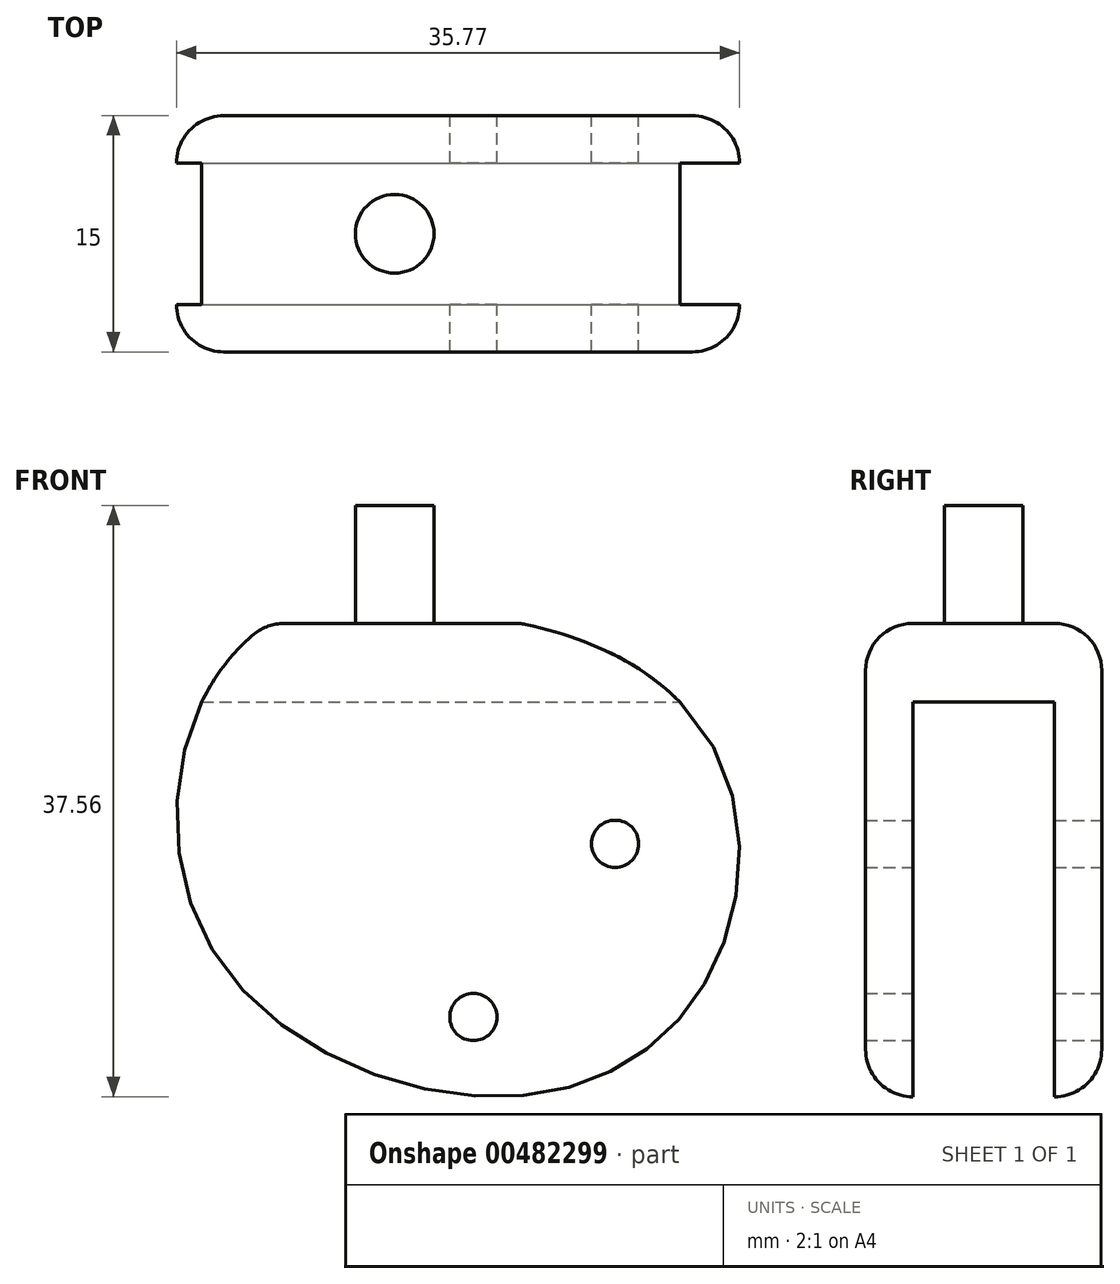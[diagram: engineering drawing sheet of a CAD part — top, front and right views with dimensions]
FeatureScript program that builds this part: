
annotation { "Feature Type Name" : "Feature", "Feature Type Description" : "" }
export const myFeature = defineFeature(function(context is Context, id is Id, definition is map)
    precondition{}
    {
        {
            var Q0;
            Q0=qCreatedBy(makeId("Front.planeOp"),FACE);
            var sketch = newSketch(context, id + "F0", { "sketchPlane" : qUnion([Q0])});
            skLineSegment(sketch, "E0", {"start": v(0, 0) * mm, "end": v(-20, 0) * mm, "construction": true});
            skLineSegment(sketch, "E1", {"start": v(0, 0) * mm, "end": v(0, 20) * mm, "construction": true});
            skLineSegment(sketch, "E2", {"start": v(0, 20) * mm, "end": v(-16, 20) * mm, "construction": true});
            skLineSegment(sketch, "E3", {"start": v(0, 0) * mm, "end": v(0, -10) * mm, "construction": true});
            skLineSegment(sketch, "E4", {"start": v(0, 0) * mm, "end": v(13, 0) * mm, "construction": true});
            skFitSpline(sketch, "E5", {"points": [v(-16, 20) * mm, v(-20, 0) * mm, v(0, -10) * mm, v(13, 0) * mm, v(0, 20) * mm], "startDerivative": vector(-72.42, -47.7) * mm, "endDerivative": vector(-152.79, 31.21) * mm});
            skLineSegment(sketch, "E6", {"start": v(-16, 20) * mm, "end": v(0, 20) * mm});
            skLineSegment(sketch, "E7.bottom", {"start": v(0, 0) * mm, "end": v(-3, 0) * mm, "construction": true});
            skLineSegment(sketch, "E7.top", {"start": v(0, -5) * mm, "end": v(-3, -5) * mm, "construction": true});
            skLineSegment(sketch, "E7.left", {"start": v(0, 0) * mm, "end": v(0, -5) * mm, "construction": true});
            skLineSegment(sketch, "E7.right", {"start": v(-3, 0) * mm, "end": v(-3, -5) * mm, "construction": true});
            skLineSegment(sketch, "E8.bottom", {"start": v(0, 0) * mm, "end": v(6, 0) * mm, "construction": true});
            skLineSegment(sketch, "E8.top", {"start": v(0, 6) * mm, "end": v(6, 6) * mm, "construction": true});
            skLineSegment(sketch, "E8.left", {"start": v(0, 0) * mm, "end": v(0, 6) * mm, "construction": true});
            skLineSegment(sketch, "E8.right", {"start": v(6, 0) * mm, "end": v(6, 6) * mm, "construction": true});
            skCircle(sketch, "E9", {"center": v(-3, -5) * mm, "radius": 1.5 * mm});
            skCircle(sketch, "E10", {"center": v(6, 6) * mm, "radius": 1.5 * mm});
            skSolve(sketch);
        }
        {
            var Q0;
            Q0=makeQuery(id+"F0.imprint","IMPRINT",FACE,{"disambiguationData":[TD([[makeQuery(id+"F0.imprint","IMPRINT",EDGE,{"derivedFrom":sQuery(id+"F0.wireOp",EDGE,"E5")}),1.0]])]});
            extrude(context, id + "F1", {"entities" : qUnion([Q0]), "depth" : 15 * mm});
        }
        {
            var Q0;
            Q0=makeQuery(id+"F1.opExtrude","SWEPT_FACE",FACE,{"disambiguationData":[OSD([sQuery(id+"F0.wireOp",EDGE,"E6")])]});
            var sketch = newSketch(context, id + "F2", { "sketchPlane" : qUnion([Q0])});
            skLineSegment(sketch, "E11", {"start": v(-8, 0) * mm, "end": v(-8, -7.5) * mm, "construction": true});
            skCircle(sketch, "E12", {"center": v(-8, -7.5) * mm, "radius": 2.5 * mm});
            skSolve(sketch);
        }
        {
            var Q0;
            Q0=makeQuery(id+"F2.imprint","IMPRINT",FACE,{"disambiguationData":[TD([[makeQuery(id+"F2.imprint","IMPRINT",EDGE,{"derivedFrom":sQuery(id+"F2.wireOp",EDGE,"E12")}),1.0]])]});
            extrude(context, id + "F3", {"entities" : qUnion([Q0]), "operationType" : NewBodyOperationType.ADD, "depth" : 7.5 * mm});
        }
        {
            var Q0;
            Q0=qCreatedBy(makeId("Right.planeOp"),FACE);
            var sketch = newSketch(context, id + "F4", { "sketchPlane" : qUnion([Q0])});
            skLineSegment(sketch, "E13", {"start": v(0, 0) * mm, "end": v(-3, 0) * mm, "construction": true});
            skLineSegment(sketch, "E14", {"start": v(-3, 0) * mm, "end": v(-3, -11) * mm, "construction": true});
            skLineSegment(sketch, "E15.bottom", {"start": v(-3, -11) * mm, "end": v(-12, -11) * mm});
            skLineSegment(sketch, "E15.top", {"start": v(-3, 15) * mm, "end": v(-12, 15) * mm});
            skLineSegment(sketch, "E15.left", {"start": v(-3, -11) * mm, "end": v(-3, 15) * mm});
            skLineSegment(sketch, "E15.right", {"start": v(-12, -11) * mm, "end": v(-12, 15) * mm});
            skSolve(sketch);
        }
        {
            var Q0;
            Q0=makeQuery(id+"F4.imprint","IMPRINT",FACE,{"disambiguationData":[TD([[makeQuery(id+"F4.imprint","IMPRINT",EDGE,{"derivedFrom":sQuery(id+"F4.wireOp",EDGE,"E15.bottom")}),-1.0]])]});
            extrude(context, id + "F5", {"entities" : qUnion([Q0]), "operationType" : NewBodyOperationType.REMOVE, "oppositeDirection" : true, "depth" : 25 * mm});
        }
        {
            var Q0;
            Q0=makeQuery(id+"F4.imprint","IMPRINT",FACE,{"disambiguationData":[TD([[makeQuery(id+"F4.imprint","IMPRINT",EDGE,{"derivedFrom":sQuery(id+"F4.wireOp",EDGE,"E15.bottom")}),-1.0]])]});
            extrude(context, id + "F6", {"entities" : qUnion([Q0]), "operationType" : NewBodyOperationType.REMOVE, "depth" : 25 * mm});
        }
        {
            var Q0;
            Q0=makeQuery(id+"F1.opExtrude","CAP_EDGE",EDGE,{"disambiguationData":[OSD([sQuery(id+"F0.wireOp",EDGE,"E6")])],"isStart":false});
            var Q1;
            Q1=makeQuery(id+"F1.opExtrude","CAP_EDGE",EDGE,{"disambiguationData":[OSD([sQuery(id+"F0.wireOp",EDGE,"E6")])],"isStart":true});
            var Q2;
            Q2=makeQuery(id+"F1.opExtrude","CAP_EDGE",EDGE,{"disambiguationData":[OSD([sQuery(id+"F0.wireOp",EDGE,"E5")])],"isStart":true});
            var Q3;
            Q3=makeQuery(id+"F1.opExtrude","CAP_EDGE",EDGE,{"disambiguationData":[OSD([sQuery(id+"F0.wireOp",EDGE,"E5")])],"isStart":false});
            var Q4;
            {var subQ0=sQuery(id+"F0.wireOp",EDGE,"E6");var subQ1=sQuery(id+"F0.wireOp",EDGE,"E5");Q4=makeQuery(id+"F1.opExtrude","SWEPT_EDGE",EDGE,{"disambiguationData":[OSD([subQ1,subQ0]),TDD([makeQuery(id+"F0.imprint","INTERSECT",VERTEX,{"disambiguationData":[OD(1.0)],"derivedFrom":[subQ1,subQ0]})])]});}
            var Q5;
            {var subQ0=sQuery(id+"F0.wireOp",EDGE,"E6");var subQ1=sQuery(id+"F0.wireOp",EDGE,"E5");Q5=makeQuery(id+"F1.opExtrude","SWEPT_EDGE",EDGE,{"disambiguationData":[OSD([subQ1,subQ0]),TDD([makeQuery(id+"F0.imprint","INTERSECT",VERTEX,{"disambiguationData":[OD(0.0)],"derivedFrom":[subQ1,subQ0]})])]});}
            fillet(context, id + "F7", {"entities" : qUnion([Q0, Q1, Q2, Q3, Q4, Q5]), "radius" : 3 * mm, "tangentPropagation" : true, "allowEdgeOverflow" : false});
        }
    });
